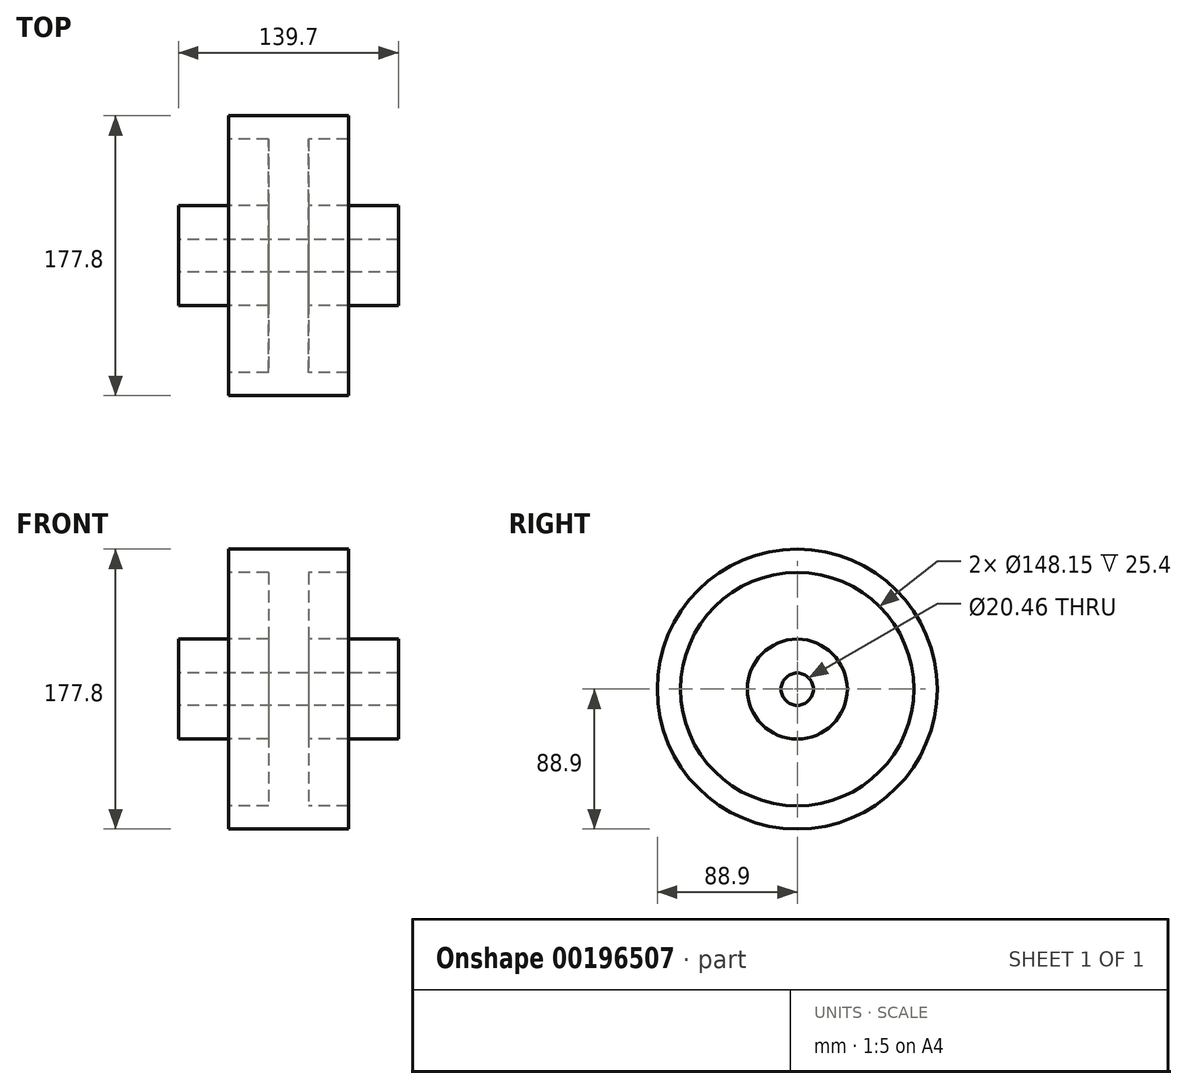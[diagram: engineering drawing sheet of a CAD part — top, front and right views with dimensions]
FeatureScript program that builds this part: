
annotation { "Feature Type Name" : "Feature", "Feature Type Description" : "" }
export const myFeature = defineFeature(function(context is Context, id is Id, definition is map)
    precondition{}
    {
        {
            var Q0;
            Q0=qCreatedBy(makeId("Front.planeOp"),FACE);
            var sketch = newSketch(context, id + "F0", { "sketchPlane" : qUnion([Q0])});
            skLineSegment(sketch, "E0", {"start": v(-72.92, 0) * mm, "end": v(73.2, 0) * mm, "construction": true});
            skLineSegment(sketch, "E1", {"start": v(0, 0) * mm, "end": v(0, 114.55) * mm, "construction": true});
            skLineSegment(sketch, "E2", {"start": v(12.7, 74.07) * mm, "end": v(38.1, 74.07) * mm});
            skLineSegment(sketch, "E3", {"start": v(38.1, 74.07) * mm, "end": v(38.1, 88.9) * mm});
            skLineSegment(sketch, "E4", {"start": v(38.1, 88.9) * mm, "end": v(-38.1, 88.9) * mm});
            skLineSegment(sketch, "E5", {"start": v(-38.1, 88.9) * mm, "end": v(-38.1, 74.07) * mm});
            skLineSegment(sketch, "E6", {"start": v(-38.1, 74.07) * mm, "end": v(-12.7, 74.07) * mm});
            skLineSegment(sketch, "E7", {"start": v(-12.7, 74.07) * mm, "end": v(-12.7, 31.75) * mm});
            skLineSegment(sketch, "E8", {"start": v(-12.7, 31.75) * mm, "end": v(-69.85, 31.75) * mm});
            skLineSegment(sketch, "E9", {"start": v(-69.85, 31.75) * mm, "end": v(-69.85, 10.23) * mm});
            skLineSegment(sketch, "E10", {"start": v(-69.85, 10.23) * mm, "end": v(69.85, 10.23) * mm});
            skLineSegment(sketch, "E11", {"start": v(69.85, 10.23) * mm, "end": v(69.85, 31.75) * mm});
            skLineSegment(sketch, "E12", {"start": v(69.85, 31.75) * mm, "end": v(12.7, 31.75) * mm});
            skLineSegment(sketch, "E13", {"start": v(12.7, 31.75) * mm, "end": v(12.7, 74.07) * mm});
            skSolve(sketch);
        }
        {
            var Q0;
            Q0=makeQuery(id+"F0.imprint","IMPRINT",FACE,{"disambiguationData":[TD([[makeQuery(id+"F0.imprint","IMPRINT",EDGE,{"derivedFrom":sQuery(id+"F0.wireOp",EDGE,"E2")}),1.0]])]});
            var Q1;
            Q1=sQuery(id+"F0.wireOp",EDGE,"E0");
            revolve(context, id + "F1", {"entities" : qUnion([Q0]), "axis" : qUnion([Q1]), "revolveType" : RevolveType.FULL});
        }
    });
